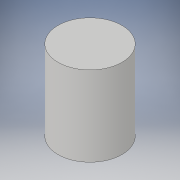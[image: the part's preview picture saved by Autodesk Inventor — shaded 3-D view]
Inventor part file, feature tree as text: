
AUTODESK INVENTOR PART (.ipt)
format: ipt  version: 2019 (Build 230136000, 136)  size: 87,552 bytes
history: native  units: mm
features: extrude x1, sketch x1
ambient origin geometry x8: Origin, YZ Plane, XZ Plane, XY Plane, X Axis, Y Axis, Z Axis, Center Point
bodies: Solid1 (feature_tree)
feature tree (2):
  extrude  "Extrusion1"  Depth=100.0mm TaperAngle=0.0deg
  sketch  "Sketch1"  dims[d0=80.0mm d1=100.0mm d2=0.0mm]
